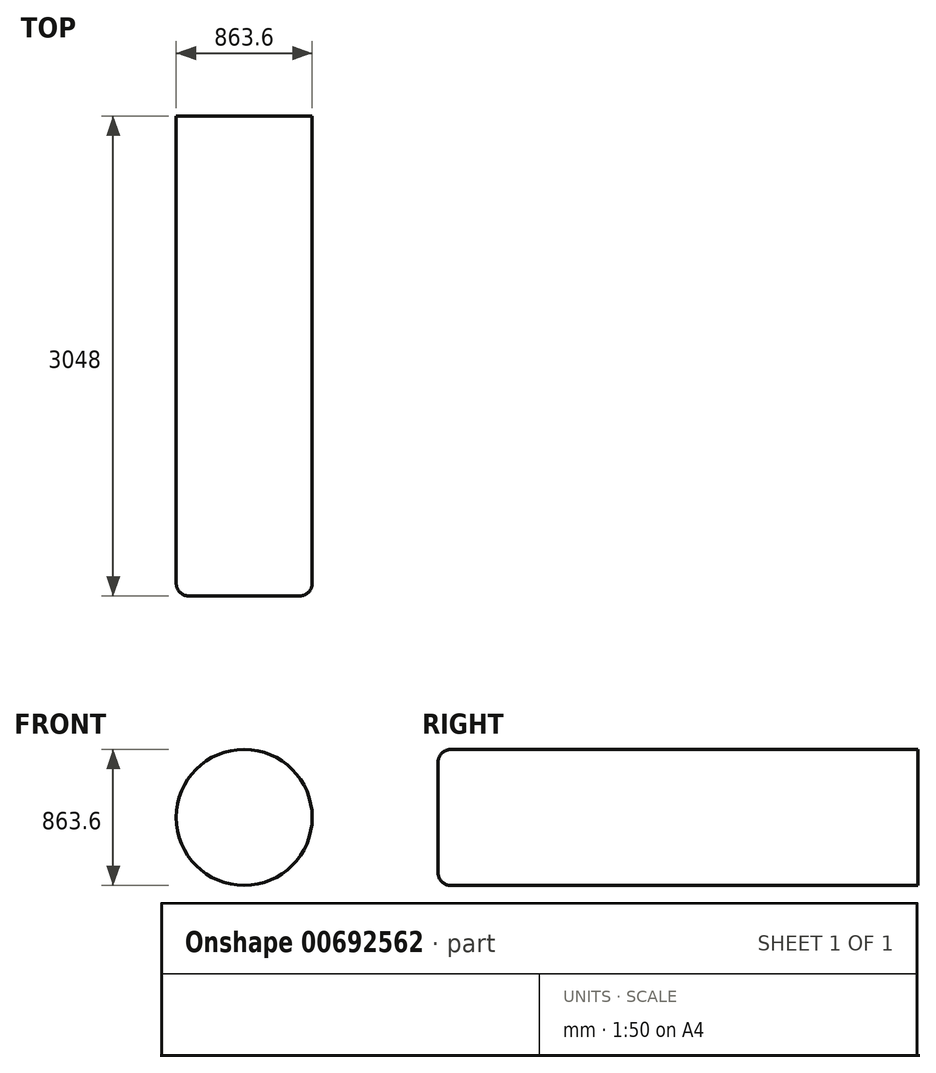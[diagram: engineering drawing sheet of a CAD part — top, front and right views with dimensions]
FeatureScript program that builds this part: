
annotation { "Feature Type Name" : "Feature", "Feature Type Description" : "" }
export const myFeature = defineFeature(function(context is Context, id is Id, definition is map)
    precondition{}
    {
        {
            var Q0;
            Q0=qCreatedBy(makeId("Front.planeOp"),FACE);
            var sketch = newSketch(context, id + "F0", { "sketchPlane" : qUnion([Q0])});
            skCircle(sketch, "E0", {"center": v(0, 0) * mm, "radius": 431.8 * mm});
            skSolve(sketch);
        }
        {
            var Q0;
            Q0 = qSketchRegion(id + "F0", true);
            var Q1;
            Q1=makeQuery(id+"F0.imprint","IMPRINT",FACE,{"disambiguationData":[TD([[makeQuery(id+"F0.imprint","IMPRINT",EDGE,{"derivedFrom":sQuery(id+"F0.wireOp",EDGE,"E0")}),1.0]])]});
            extrude(context, id + "F1", {"entities" : qUnion([Q0, Q1]), "depth" : 3048 * mm, "offsetDistance" : 25.4 * mm});
        }
        {
            var Q0;
            Q0=makeQuery(id+"F1.opExtrude","CAP_EDGE",EDGE,{"disambiguationData":[OSD([sQuery(id+"F0.wireOp",EDGE,"E0")])],"isStart":false});
            fillet(context, id + "F2", {"entities" : qUnion([Q0]), "radius" : 79.72 * mm, "tangentPropagation" : true, "allowEdgeOverflow" : false});
        }
    });
